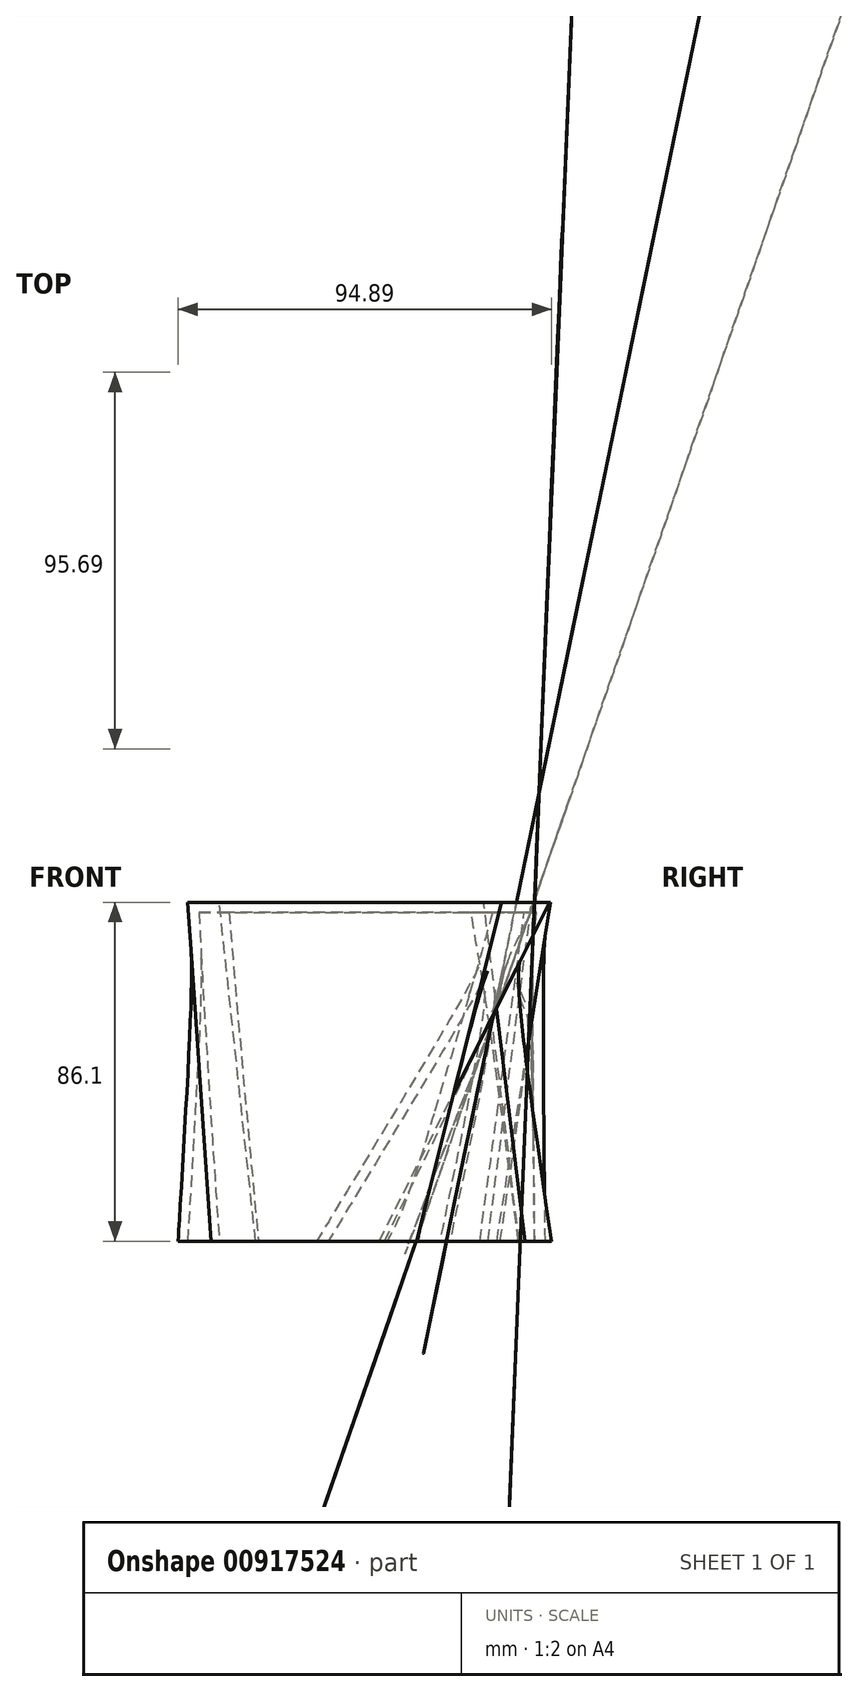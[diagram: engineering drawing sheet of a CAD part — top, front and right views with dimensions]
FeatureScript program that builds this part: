
annotation { "Feature Type Name" : "Feature", "Feature Type Description" : "" }
export const myFeature = defineFeature(function(context is Context, id is Id, definition is map)
    precondition{}
    {
        {
            var Q0;
            Q0=qCreatedBy(makeId("Top.planeOp"),FACE);
            var sketch = newSketch(context, id + "F0", { "sketchPlane" : qUnion([Q0])});
            skFitSpline(sketch, "E0", {"points": [v(20.98, 25.98) * mm, v(-35.77, 43.8) * mm, v(-45.33, -4.67) * mm, v(9.24, -47.94) * mm, v(-13.15, -22.72) * mm, v(42.94, -44.68) * mm, v(19.68, -18.59) * mm, v(19.24, -12.28) * mm, v(39.68, -16.2) * mm, v(20.98, 25.98) * mm]});
            skSolve(sketch);
        }
        {
            var Q0;
            Q0=makeQuery(id+"F0.imprint","IMPRINT",FACE,{"disambiguationData":[TD([[makeQuery(id+"F0.imprint","IMPRINT",EDGE,{"derivedFrom":sQuery(id+"F0.wireOp",EDGE,"E0")}),1.0]])]});
            cPlane(context, id + "F1", {"entities" : qUnion([Q0]), "cplaneType" : CPlaneType.OFFSET, "offset" : 86.1 * mm, "width" : 152.4 * mm, "height" : 152.4 * mm});
        }
        {
            var Q0;
            Q0=qCreatedBy(id+"F1.planeOp",FACE);
            var sketch = newSketch(context, id + "F2", { "sketchPlane" : qUnion([Q0])});
            skLineSegment(sketch, "E1", {"start": v(38.37, 27.5) * mm, "end": v(-40.98, 45.98) * mm});
            skLineSegment(sketch, "E2", {"start": v(-40.98, 45.98) * mm, "end": v(-49.03, -26.63) * mm});
            skLineSegment(sketch, "E3", {"start": v(-49.03, -26.63) * mm, "end": v(30.76, -45.33) * mm});
            skLineSegment(sketch, "E4", {"start": v(30.76, -45.33) * mm, "end": v(42.94, -16.2) * mm});
            skLineSegment(sketch, "E5", {"start": v(42.94, -16.2) * mm, "end": v(26.2, 0) * mm});
            skLineSegment(sketch, "E6", {"start": v(26.2, 0) * mm, "end": v(43.16, 20.55) * mm});
            skLineSegment(sketch, "E7", {"start": v(43.16, 20.55) * mm, "end": v(38.37, 27.5) * mm});
            skSolve(sketch);
        }
        {
            var Q0;
            Q0=makeQuery(id+"F0.imprint","IMPRINT",FACE,{"disambiguationData":[TD([[makeQuery(id+"F0.imprint","IMPRINT",EDGE,{"derivedFrom":sQuery(id+"F0.wireOp",EDGE,"E0")}),1.0]])]});
            var Q1;
            Q1=makeQuery(id+"F2.imprint","IMPRINT",FACE,{"disambiguationData":[TD([[makeQuery(id+"F2.imprint","IMPRINT",EDGE,{"derivedFrom":sQuery(id+"F2.wireOp",EDGE,"E1")}),1.0]])]});
            loft(context, id + "F3", {"sheetProfilesArray" : [{ "sheetProfileEntities" : qUnion([Q0]) }, { "sheetProfileEntities" : qUnion([Q1]) }]});
        }
        {
            var Q0;
            Q0=makeQuery(id+"F3.opLoft","CAP_FACE",FACE,{"disambiguationData":[OSD([makeQuery(id+"F0.imprint","IMPRINT",FACE,{"disambiguationData":[TD([[makeQuery(id+"F0.imprint","IMPRINT",EDGE,{"derivedFrom":sQuery(id+"F0.wireOp",EDGE,"E0")}),1.0]])]})])],"isStart":true});
            shell(context, id + "F4", {"entities" : qUnion([Q0]), "thickness" : 2.54 * mm});
        }
    });
